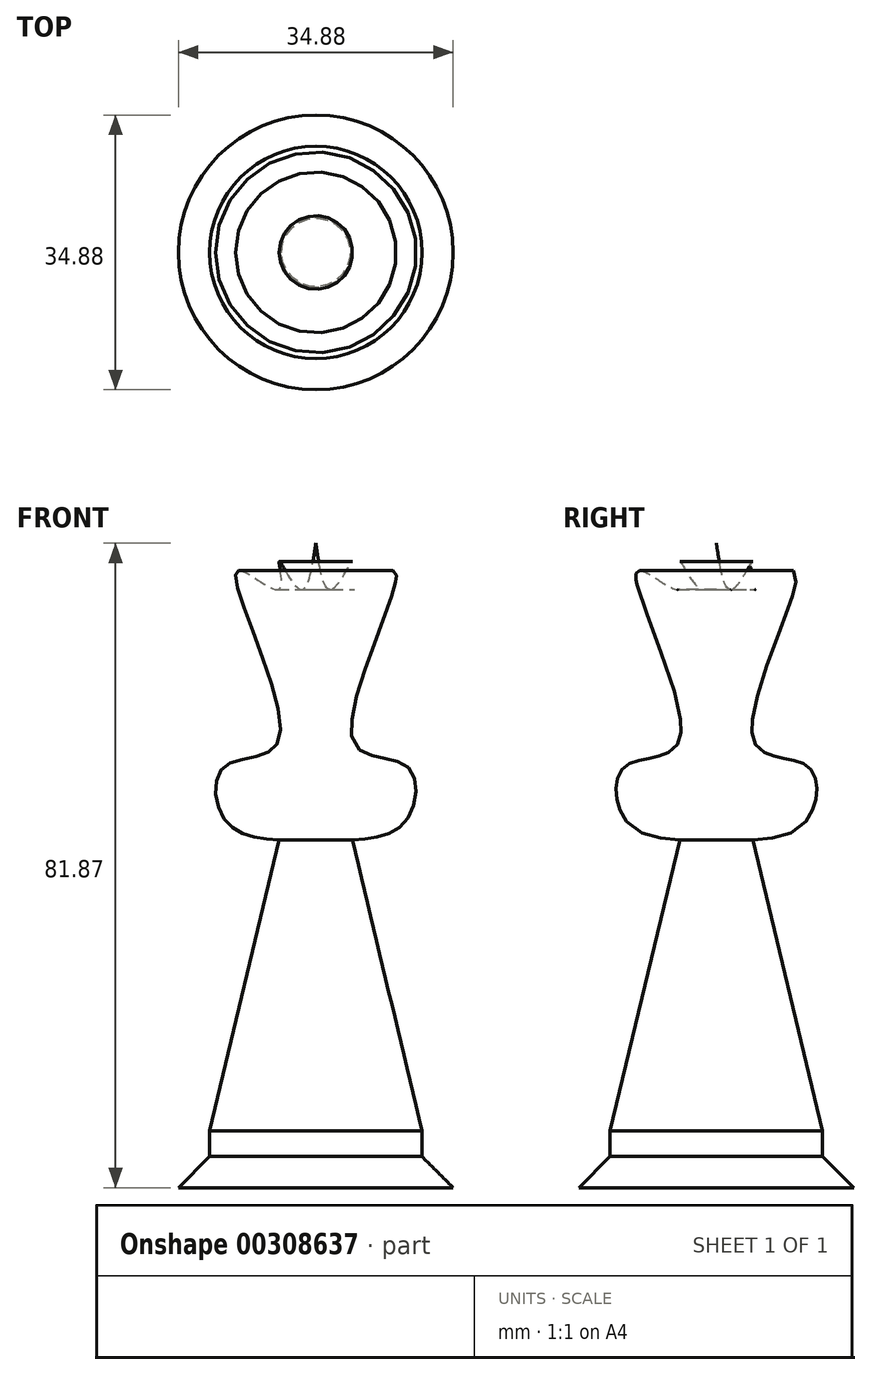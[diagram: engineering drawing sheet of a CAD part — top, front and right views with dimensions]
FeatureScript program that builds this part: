
annotation { "Feature Type Name" : "Feature", "Feature Type Description" : "" }
export const myFeature = defineFeature(function(context is Context, id is Id, definition is map)
    precondition{}
    {
        {
            var Q0;
            Q0=qCreatedBy(makeId("Front.planeOp"),FACE);
            var sketch = newSketch(context, id + "F0", { "sketchPlane" : qUnion([Q0])});
            skLineSegment(sketch, "E0", {"start": v(0, 41.17) * mm, "end": v(0, -40.7) * mm});
            skLineSegment(sketch, "E1", {"start": v(0, -40.7) * mm, "end": v(-17.44, -40.7) * mm});
            skLineSegment(sketch, "E2", {"start": v(-17.44, -40.7) * mm, "end": v(-13.5, -36.75) * mm});
            skLineSegment(sketch, "E3", {"start": v(-13.5, -36.75) * mm, "end": v(-13.5, -33.5) * mm});
            skLineSegment(sketch, "E4", {"start": v(-13.5, -33.5) * mm, "end": v(-4.65, 3.49) * mm});
            skFitSpline(sketch, "E5", {"points": [v(-4.65, 3.49) * mm, v(-11.4, 5.81) * mm, v(-11.63, 12.8) * mm, v(-4.65, 16.28) * mm, v(-10, 37.68) * mm, v(-4.65, 35.35) * mm, v(-4.65, 38.84) * mm, v(-2.1, 35.35) * mm, v(0, 41.17) * mm], "startDerivative": vector(-63.4, 4.72) * mm, "endDerivative": vector(12.37, 83.8) * mm});
            skSolve(sketch);
        }
        {
            var Q0;
            Q0 = qSketchRegion(id + "F0", true);
            var Q1;
            Q1=sQuery(id+"F0.wireOp",EDGE,"E0");
            revolve(context, id + "F1", {"entities" : qUnion([Q0]), "axis" : qUnion([Q1]), "revolveType" : RevolveType.FULL});
        }
    });
